# Revit family: GMV-ND（40-63）PLSC1-T
name_source: partatom
category: 机械设备
revit_build: Autodesk Revit 2014 (Build: 20130308_1515(x64)
units: mm (PartAtom-declared; Revit-internal decimal feet)

## types (5) — shared parameters
Depth = 462  [stored 1.51575 ft]
Hight = 200  [stored 0.656168 ft]
Highth = 200  [stored 0.656168 ft]
Width = 1010  [stored 3.31365 ft]
净重(kg) = 25
回风口宽度 = 979  [stored 3.21194 ft]
回风口高度 = 175  [stored 0.574147 ft]
定位孔（宽） = 1060  [stored 3.47769 ft]
定位孔（深） = 415  [stored 1.36155 ft]
宽 = 1010  [stored 3.31365 ft]
排水管管径 = 25  [stored 0.082021 ft]
深 = 462  [stored 1.51575 ft]
电源 = 220V~50Hz
送风口宽度 = 885
送风口高度 = 122  [stored 0.400262 ft]
高 = 200  [stored 0.656168 ft]

## per-type parameters (varying)
| type | 气管管径 | 液管管径 |
| GMV-ND40PLS/C1-T | 12.7  [stored 0.0416667 ft] | 6.35  [stored 0.0208333 ft] |
| GMV-ND45PLS/C1-T | 12.7  [stored 0.0416667 ft] | 6.35  [stored 0.0208333 ft] |
| GMV-ND50PLS/C1-T | 12.7  [stored 0.0416667 ft] | 6.35  [stored 0.0208333 ft] |
| GMV-ND56PLS/C1-T | 15.9  [stored 0.0521654 ft] | 9.52 |
| GMV-ND63PLS/C1-T | 15.9  [stored 0.0521654 ft] | 9.5  [stored 0.031168 ft] |

note: [stored X ft] marks values corroborated as IEEE doubles in the binary element streams (Revit-internal decimal feet)
